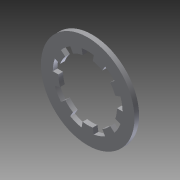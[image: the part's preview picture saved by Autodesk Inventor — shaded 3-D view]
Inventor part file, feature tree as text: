
AUTODESK INVENTOR PART (.ipt)
format: ipt  version: 2014 (Build 180170000, 170)  size: 127,488 bytes
history: native  units: in
note: dims shown in document units (in); Inventor stores cm internally (conversion verified against a paired STEP export)
features: other x7, extrude x1, sketch x1
ambient origin geometry x8: Origin, YZ Plane, XZ Plane, XY Plane, X Axis, Y Axis, Z Axis, Center Point
bodies: Solid1 (feature_tree)
feature tree (9):
  extrude  "Extrusion1"  [1 undecoded]
  other  "lockwasher_XY"
  other  "lockwasher_YZ"
  other  "lockwasher_ZX"
  other  "lockwasher_X"
  other  "lockwasher_Y"
  other  "lockwasher_Z"
  other  "lockwasher_Center"
  sketch  "Sketch_2"  dims[d0=0.02in d1=0.0in]
note: 1 required parameter value undecoded (feature->parameter linkage not recoverable at this tier; creation-order binding heuristic only, values carry confidence <= 0.55)
